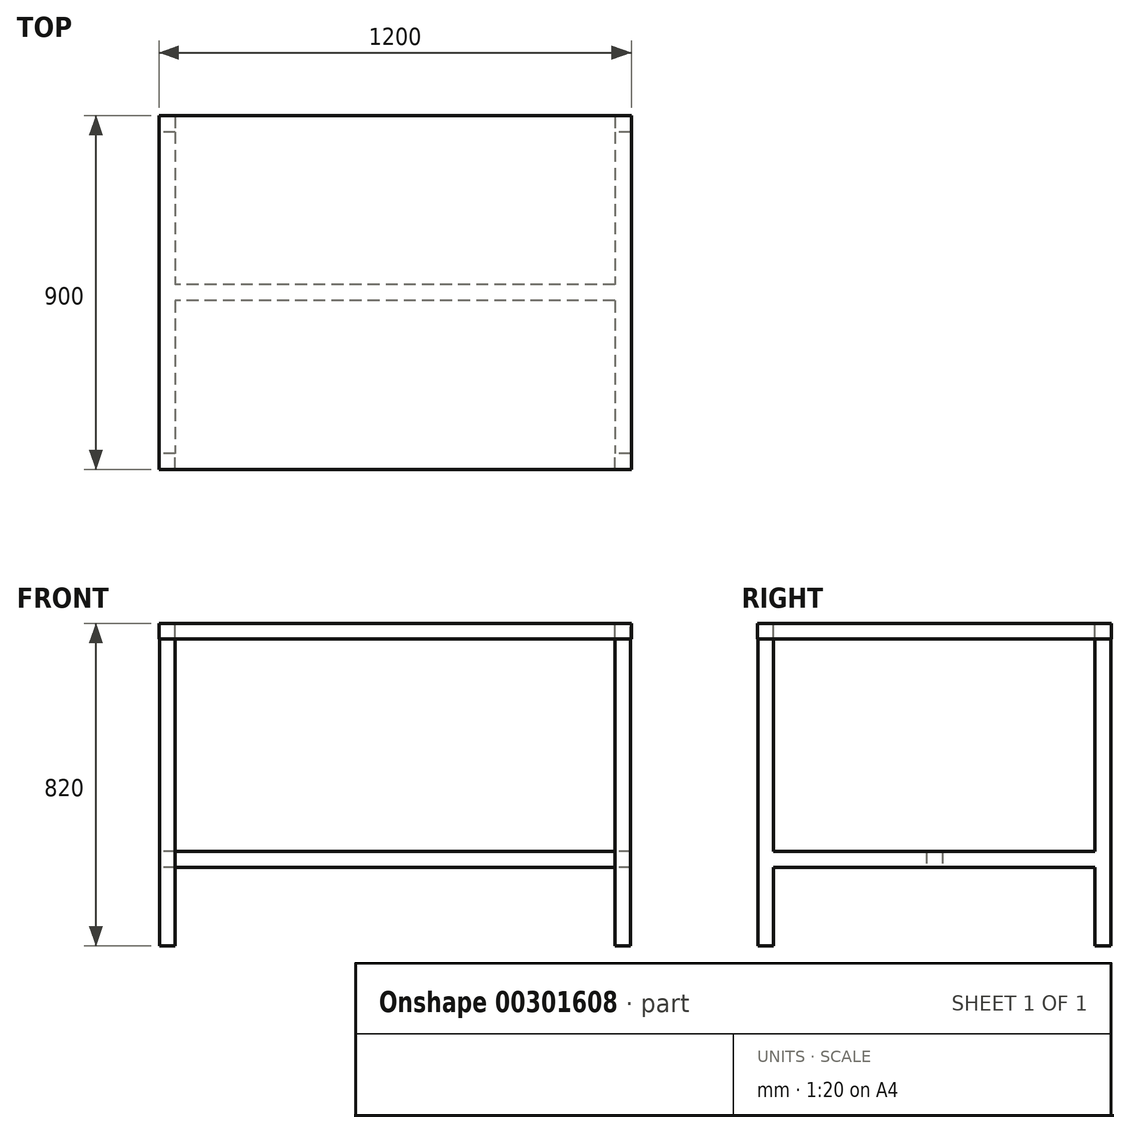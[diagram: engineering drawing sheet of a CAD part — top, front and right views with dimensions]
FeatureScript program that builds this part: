
annotation { "Feature Type Name" : "Feature", "Feature Type Description" : "" }
export const myFeature = defineFeature(function(context is Context, id is Id, definition is map)
    precondition{}
    {
        {
            var Q0;
            Q0=qCreatedBy(makeId("Top.planeOp"),FACE);
            var sketch = newSketch(context, id + "F0", { "sketchPlane" : qUnion([Q0])});
            skLineSegment(sketch, "E0.bottom", {"start": v(600, 450) * mm, "end": v(-600, 450) * mm});
            skLineSegment(sketch, "E0.top", {"start": v(600, -450) * mm, "end": v(-600, -450) * mm});
            skLineSegment(sketch, "E0.left", {"start": v(600, 450) * mm, "end": v(600, -450) * mm});
            skLineSegment(sketch, "E0.right", {"start": v(-600, 450) * mm, "end": v(-600, -450) * mm});
            skPoint(sketch, "E0.middle", {"position": v(0, 0) * mm});
            skSolve(sketch);
        }
        {
            var Q0;
            Q0 = qSketchRegion(id + "F0", true);
            extrude(context, id + "F1", {"entities" : qUnion([Q0]), "depth" : 40 * mm});
        }
        {
            var Q0;
            Q0=makeQuery(id+"F1.opExtrude","CAP_FACE",FACE,{"disambiguationData":[OSD([sQuery(id+"F0.wireOp",EDGE,"E0.bottom"),sQuery(id+"F0.wireOp",EDGE,"E0.top"),sQuery(id+"F0.wireOp",EDGE,"E0.left"),sQuery(id+"F0.wireOp",EDGE,"E0.right")])],"isStart":true});
            shell(context, id + "F2", {"entities" : qUnion([Q0]), "thickness" : 1.5 * mm});
        }
        {
            var Q0;
            Q0=makeQuery(id+"F2.opShell","OFFSET_FACE",FACE,{"disambiguationData":[OSD([sQuery(id+"F0.wireOp",EDGE,"E0.bottom"),sQuery(id+"F0.wireOp",EDGE,"E0.top"),sQuery(id+"F0.wireOp",EDGE,"E0.left"),sQuery(id+"F0.wireOp",EDGE,"E0.right")])]});
            var sketch = newSketch(context, id + "F3", { "sketchPlane" : qUnion([Q0])});
            skLineSegment(sketch, "E1.bottom", {"start": v(-598.5, 448.5) * mm, "end": v(-558.5, 448.5) * mm});
            skLineSegment(sketch, "E1.top", {"start": v(-598.5, 408.5) * mm, "end": v(-558.5, 408.5) * mm});
            skLineSegment(sketch, "E1.left", {"start": v(-598.5, 448.5) * mm, "end": v(-598.5, 408.5) * mm});
            skLineSegment(sketch, "E1.right", {"start": v(-558.5, 448.5) * mm, "end": v(-558.5, 408.5) * mm});
            skLineSegment(sketch, "E2.bottom", {"start": v(598.5, 448.5) * mm, "end": v(558.5, 448.5) * mm});
            skLineSegment(sketch, "E2.top", {"start": v(598.5, 408.5) * mm, "end": v(558.5, 408.5) * mm});
            skLineSegment(sketch, "E2.left", {"start": v(598.5, 448.5) * mm, "end": v(598.5, 408.5) * mm});
            skLineSegment(sketch, "E2.right", {"start": v(558.5, 448.5) * mm, "end": v(558.5, 408.5) * mm});
            skLineSegment(sketch, "E3.bottom", {"start": v(598.5, -448.5) * mm, "end": v(558.5, -448.5) * mm});
            skLineSegment(sketch, "E3.top", {"start": v(598.5, -408.5) * mm, "end": v(558.5, -408.5) * mm});
            skLineSegment(sketch, "E3.left", {"start": v(598.5, -448.5) * mm, "end": v(598.5, -408.5) * mm});
            skLineSegment(sketch, "E3.right", {"start": v(558.5, -448.5) * mm, "end": v(558.5, -408.5) * mm});
            skLineSegment(sketch, "E4.bottom", {"start": v(-598.5, -448.5) * mm, "end": v(-558.5, -448.5) * mm});
            skLineSegment(sketch, "E4.top", {"start": v(-598.5, -408.5) * mm, "end": v(-558.5, -408.5) * mm});
            skLineSegment(sketch, "E4.left", {"start": v(-598.5, -448.5) * mm, "end": v(-598.5, -408.5) * mm});
            skLineSegment(sketch, "E4.right", {"start": v(-558.5, -448.5) * mm, "end": v(-558.5, -408.5) * mm});
            skSolve(sketch);
        }
        {
            var Q0;
            Q0 = qSketchRegion(id + "F3", true);
            extrude(context, id + "F4", {"entities" : qUnion([Q0]), "operationType" : NewBodyOperationType.ADD, "depth" : 818.5 * mm});
        }
        {
            var Q0;
            Q0=makeQuery(id+"F4.opExtrude","SWEPT_FACE",FACE,{"disambiguationData":[OSD([sQuery(id+"F3.wireOp",EDGE,"E3.right")])]});
            var sketch = newSketch(context, id + "F5", { "sketchPlane" : qUnion([Q0])});
            skLineSegment(sketch, "E5.bottom", {"start": v(-408.5, -580) * mm, "end": v(408.5, -580) * mm});
            skLineSegment(sketch, "E5.top", {"start": v(-408.5, -540) * mm, "end": v(408.5, -540) * mm});
            skLineSegment(sketch, "E5.left", {"start": v(-408.5, -580) * mm, "end": v(-408.5, -540) * mm});
            skLineSegment(sketch, "E5.right", {"start": v(408.5, -580) * mm, "end": v(408.5, -540) * mm});
            skSolve(sketch);
        }
        {
            var Q0;
            Q0 = qSketchRegion(id + "F5", true);
            extrude(context, id + "F6", {"entities" : qUnion([Q0]), "operationType" : NewBodyOperationType.ADD, "oppositeDirection" : true, "depth" : 40 * mm});
        }
        {
            var Q0;
            Q0=makeQuery(id+"F4.opExtrude","SWEPT_FACE",FACE,{"disambiguationData":[OSD([sQuery(id+"F3.wireOp",EDGE,"E4.left")])]});
            var sketch = newSketch(context, id + "F7", { "sketchPlane" : qUnion([Q0])});
            skLineSegment(sketch, "E6.bottom", {"start": v(-408.5, -580) * mm, "end": v(408.5, -580) * mm});
            skLineSegment(sketch, "E6.top", {"start": v(-408.5, -540) * mm, "end": v(408.5, -540) * mm});
            skLineSegment(sketch, "E6.left", {"start": v(-408.5, -580) * mm, "end": v(-408.5, -540) * mm});
            skLineSegment(sketch, "E6.right", {"start": v(408.5, -580) * mm, "end": v(408.5, -540) * mm});
            skSolve(sketch);
        }
        {
            var Q0;
            Q0 = qSketchRegion(id + "F7", true);
            extrude(context, id + "F8", {"entities" : qUnion([Q0]), "operationType" : NewBodyOperationType.ADD, "oppositeDirection" : true, "depth" : 40 * mm});
        }
        {
            var Q0;
            Q0=makeQuery(id+"F8.opExtrude","SWEPT_FACE",FACE,{"disambiguationData":[OSD([sQuery(id+"F7.wireOp",EDGE,"E6.bottom")])]});
            var sketch = newSketch(context, id + "F9", { "sketchPlane" : qUnion([Q0])});
            skLineSegment(sketch, "E7.bottom", {"start": v(558.5, 20) * mm, "end": v(-558.5, 20) * mm});
            skLineSegment(sketch, "E7.top", {"start": v(558.5, -20) * mm, "end": v(-558.5, -20) * mm});
            skLineSegment(sketch, "E7.left", {"start": v(558.5, 20) * mm, "end": v(558.5, -20) * mm});
            skLineSegment(sketch, "E7.right", {"start": v(-558.5, 20) * mm, "end": v(-558.5, -20) * mm});
            skPoint(sketch, "E7.middle", {"position": v(0, 0) * mm});
            skSolve(sketch);
        }
        {
            var Q0;
            Q0 = qSketchRegion(id + "F9", true);
            extrude(context, id + "F10", {"entities" : qUnion([Q0]), "operationType" : NewBodyOperationType.ADD, "oppositeDirection" : true, "depth" : 40 * mm});
        }
    });
